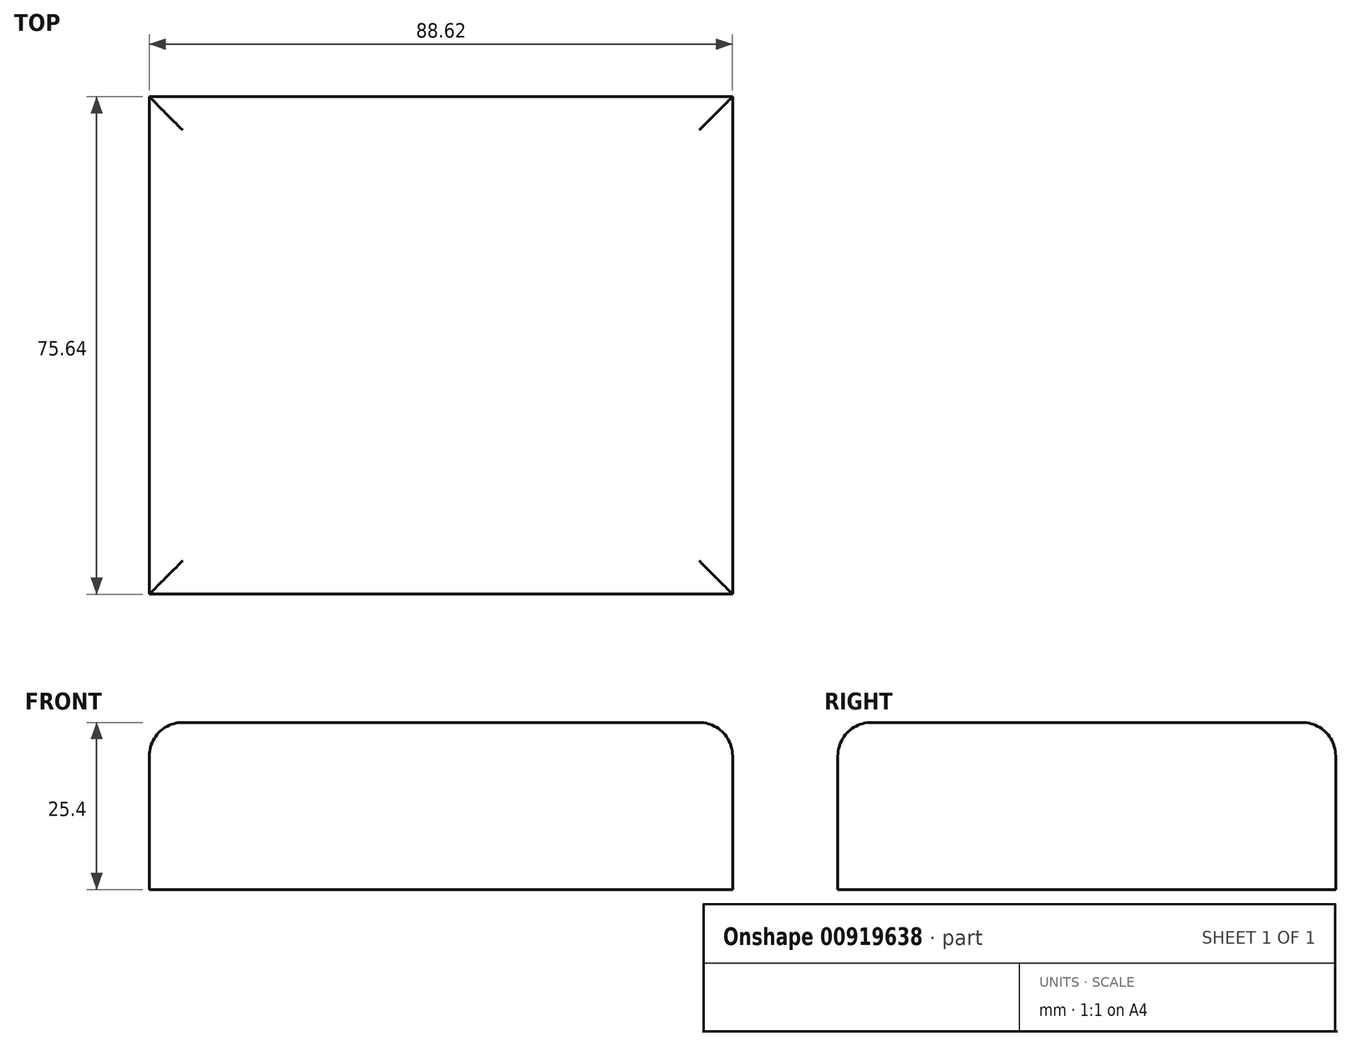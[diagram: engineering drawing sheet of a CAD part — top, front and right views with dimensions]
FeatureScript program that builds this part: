
annotation { "Feature Type Name" : "Feature", "Feature Type Description" : "" }
export const myFeature = defineFeature(function(context is Context, id is Id, definition is map)
    precondition{}
    {
        {
            var Q0;
            Q0=qCreatedBy(makeId("Top.planeOp"),FACE);
            var sketch = newSketch(context, id + "F0", { "sketchPlane" : qUnion([Q0])});
            skLineSegment(sketch, "E0.bottom", {"start": v(44.31, -37.82) * mm, "end": v(-44.31, -37.82) * mm});
            skLineSegment(sketch, "E0.top", {"start": v(44.31, 37.82) * mm, "end": v(-44.31, 37.82) * mm});
            skLineSegment(sketch, "E0.left", {"start": v(44.31, -37.82) * mm, "end": v(44.31, 37.82) * mm});
            skLineSegment(sketch, "E0.right", {"start": v(-44.31, -37.82) * mm, "end": v(-44.31, 37.82) * mm});
            skPoint(sketch, "E0.middle", {"position": v(0, 0) * mm});
            skSolve(sketch);
        }
        {
            var Q0;
            Q0=makeQuery(id+"F0.imprint","IMPRINT",FACE,{"disambiguationData":[TD([[makeQuery(id+"F0.imprint","IMPRINT",EDGE,{"derivedFrom":sQuery(id+"F0.wireOp",EDGE,"E0.bottom")}),-1.0]])]});
            extrude(context, id + "F1", {"entities" : qUnion([Q0]), "depth" : 25.4 * mm, "offsetDistance" : 25.4 * mm});
        }
        {
            var Q0;
            Q0=makeQuery(id+"F1.opExtrude","CAP_EDGE",EDGE,{"disambiguationData":[OSD([sQuery(id+"F0.wireOp",EDGE,"E0.top")])],"isStart":false});
            var Q1;
            Q1=makeQuery(id+"F1.opExtrude","CAP_EDGE",EDGE,{"disambiguationData":[OSD([sQuery(id+"F0.wireOp",EDGE,"E0.right")])],"isStart":false});
            var Q2;
            Q2=makeQuery(id+"F1.opExtrude","CAP_EDGE",EDGE,{"disambiguationData":[OSD([sQuery(id+"F0.wireOp",EDGE,"E0.left")])],"isStart":false});
            var Q3;
            Q3=makeQuery(id+"F1.opExtrude","CAP_EDGE",EDGE,{"disambiguationData":[OSD([sQuery(id+"F0.wireOp",EDGE,"E0.bottom")])],"isStart":false});
            fillet(context, id + "F2", {"entities" : qUnion([Q0, Q1, Q2, Q3]), "radius" : 5.08 * mm, "tangentPropagation" : true, "allowEdgeOverflow" : false});
        }
    });
